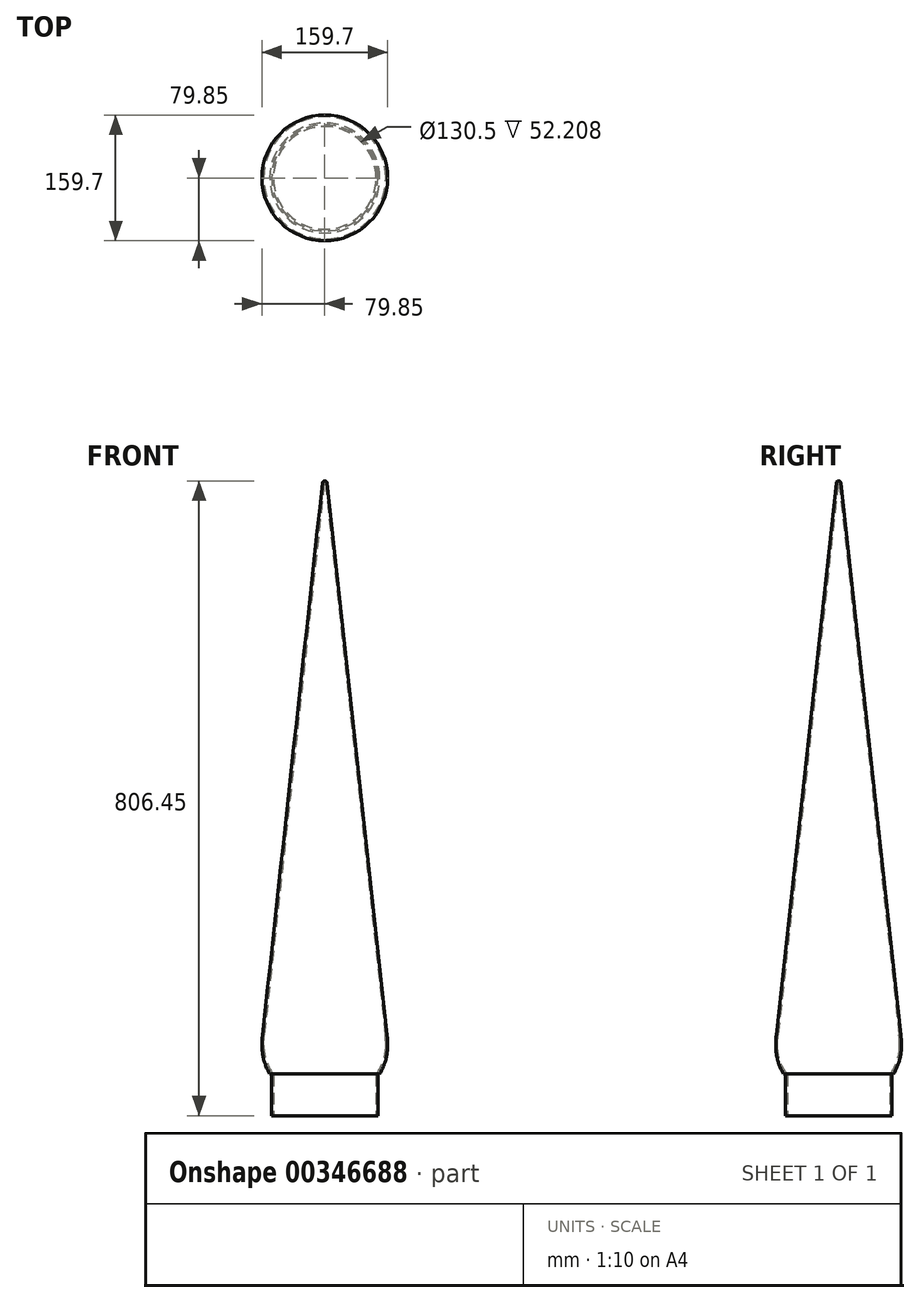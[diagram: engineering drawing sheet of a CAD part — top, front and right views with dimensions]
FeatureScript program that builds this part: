
annotation { "Feature Type Name" : "Feature", "Feature Type Description" : "" }
export const myFeature = defineFeature(function(context is Context, id is Id, definition is map)
    precondition{}
    {
        {
            var Q0;
            Q0=qCreatedBy(makeId("Front.planeOp"),FACE);
            var sketch = newSketch(context, id + "F0", { "sketchPlane" : qUnion([Q0])});
            skLineSegment(sketch, "E0", {"start": v(0, 0) * mm, "end": v(0, 806.45) * mm});
            skLineSegment(sketch, "E1", {"start": v(0, 806.45) * mm, "end": v(139.7, 806.45) * mm});
            skLineSegment(sketch, "E2", {"start": v(139.7, 806.45) * mm, "end": v(139.7, 0) * mm});
            skLineSegment(sketch, "E3", {"start": v(139.7, 0) * mm, "end": v(0, 0) * mm});
            skLineSegment(sketch, "E4", {"start": v(69.85, 0) * mm, "end": v(69.85, 806.45) * mm});
            skLineSegment(sketch, "E5", {"start": v(69.85, 806.45) * mm, "end": v(69.85, 803.45) * mm});
            skArc(sketch, "E6", {"start": v(69.85, 806.45) * mm, "mid": v(67.85, 805.68) * mm, "end": v(66.87, 803.77) * mm});
            skLineSegment(sketch, "E7", {"start": v(69.85, 0) * mm, "end": v(2.35, 0) * mm});
            skLineSegment(sketch, "E8", {"start": v(2.35, 0) * mm, "end": v(2.35, 52.64) * mm});
            skLineSegment(sketch, "E9", {"start": v(1.99, 53) * mm, "end": v(0, 53) * mm});
            skPoint(sketch, "E10.visualSharp", {"position": v(2.35, 53) * mm});
            skArc(sketch, "E10.filletArc", {"start": v(2.35, 52.64) * mm, "mid": v(2.24, 52.9) * mm, "end": v(1.99, 53) * mm});
            skLineSegment(sketch, "E11", {"start": v(0, 53) * mm, "end": v(-10, 53) * mm});
            skLineSegment(sketch, "E12", {"start": v(-10, 53) * mm, "end": v(-10, 89.12) * mm});
            skLineSegment(sketch, "E13", {"start": v(-9.26, 102.84) * mm, "end": v(66.87, 803.77) * mm});
            skPoint(sketch, "E14.visualSharp", {"position": v(-10, 96) * mm});
            skArc(sketch, "E14.filletArc", {"start": v(-9.26, 102.84) * mm, "mid": v(-9.81, 95.99) * mm, "end": v(-10, 89.12) * mm});
            skArc(sketch, "E15", {"start": v(-10, 89.12) * mm, "mid": v(-7.45, 70.38) * mm, "end": v(0, 53) * mm});
            skLineSegment(sketch, "E16", {"start": v(2.35, 0) * mm, "end": v(4.6, 0) * mm});
            skLineSegment(sketch, "E17", {"start": v(4.6, 0) * mm, "end": v(4.6, 52.2) * mm});
            skLineSegment(sketch, "E18", {"start": v(-10, 89.12) * mm, "end": v(-7.75, 89.12) * mm});
            skArc(sketch, "E19", {"start": v(-7.75, 89.12) * mm, "mid": v(-4.65, 70.06) * mm, "end": v(4.34, 52.97) * mm});
            skLineSegment(sketch, "E20", {"start": v(-7.75, 89.12) * mm, "end": v(-7.75, 95.87) * mm});
            skArc(sketch, "E21.0", {"start": v(69.85, 804.2) * mm, "mid": v(69.35, 804) * mm, "end": v(69.1, 803.53) * mm});
            skLineSegment(sketch, "E22.0", {"start": v(-7.02, 102.6) * mm, "end": v(69.1, 803.53) * mm});
            skArc(sketch, "E22.1", {"start": v(-7.02, 102.6) * mm, "mid": v(-7.57, 95.87) * mm, "end": v(-7.75, 89.12) * mm});
            skPoint(sketch, "E23.visualSharp", {"position": v(4.6, 52.64) * mm});
            skArc(sketch, "E23.filletArc", {"start": v(4.6, 52.2) * mm, "mid": v(4.53, 52.61) * mm, "end": v(4.34, 52.97) * mm});
            skSolve(sketch);
        }
        {
            var Q0;
            Q0=makeQuery(id+"F0.imprint","IMPRINT",FACE,{"disambiguationData":[TD([[makeQuery(id+"F0.imprint","IMPRINT",EDGE,{"derivedFrom":sQuery(id+"F0.wireOp",EDGE,"E8")}),-1.0]])]});
            var Q1;
            {var subQ0=sQuery(id+"F0.wireOp",EDGE,"E15");Q1=makeQuery(id+"F0.imprint","IMPRINT",FACE,{"disambiguationData":[TD([[makeQuery(id+"F0.imprint","IMPRINT",EDGE,{"derivedFrom":subQ0}),1.0]])]});}
            var Q2;
            {var subQ0=sQuery(id+"F0.wireOp",EDGE,"E14.filletArc");Q2=makeQuery(id+"F0.imprint","IMPRINT",FACE,{"disambiguationData":[TD([[makeQuery(id+"F0.imprint","IMPRINT",EDGE,{"derivedFrom":subQ0}),1.0]])]});}
            var Q3;
            {var subQ1=sQuery(id+"F0.wireOp",EDGE,"E6");Q3=makeQuery(id+"F0.imprint","IMPRINT",FACE,{"disambiguationData":[TD([[makeQuery(id+"F0.imprint","IMPRINT",EDGE,{"derivedFrom":subQ1}),1.0]])]});}
            var Q4;
            Q4=sQuery(id+"F0.wireOp",EDGE,"E4");
            revolve(context, id + "F1", {"entities" : qUnion([Q0, Q1, Q2, Q3]), "axis" : qUnion([Q4]), "revolveType" : RevolveType.FULL});
        }
    });
